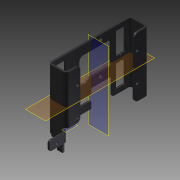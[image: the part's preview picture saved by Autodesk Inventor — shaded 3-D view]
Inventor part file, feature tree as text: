
AUTODESK INVENTOR PART (.ipt)
format: ipt  version: 2015 (Build 190159000, 159)  size: 621,056 bytes
history: native  units: mm
features: extrude x16, hole x10, fillet x7, projected_geometry x4, plane x2, other x2, mirror x1
ambient origin geometry x8: Origin, YZ Plane, XZ Plane, XY Plane, X Axis, Y Axis, Z Axis, Center Point
bodies: Solid1 (feature_tree)
feature tree (42):
  extrude  "Extrusión1"  Depth=15.0mm
  fillet  "Empalme1"  Radius=8.0mm
  extrude  "Extrusión2"  Depth=65.0mm
  hole  "Agujero1"  [1 undecoded]
  extrude  "Extrusión3"  Depth=2.0mm
  hole  "Agujero10"  [1 undecoded]
  extrude  "Extrusión21"  Depth=2.0mm
  extrude  "Extrusión22"  Depth=20.0mm
  fillet  "Empalme6"  Radius=3.0mm
  extrude  "Extrusión23"  Depth=10.11138mm TaperAngle=0.0deg
  fillet  "Empalme7"  Radius=4.0mm
  extrude  "Extrusión25"  Depth=10.11138mm
  fillet  "Empalme8"  Radius=65.0mm
  plane  "Plano de trabajo2"
  extrude  "Extrusión26"  Depth=24.2mm
  hole  "Agujero12"  [1 undecoded]
  fillet  "Empalme9"  Radius=10.0mm
  hole  "Agujero13"  [1 undecoded]
  hole  "Agujero14"  [1 undecoded]
  extrude  "Extrusión27"  Depth=35.0mm
  hole  "Agujero2"  [1 undecoded]
  hole  "Agujero3"  [1 undecoded]
  extrude  "Extrusión5"  Depth=10.0mm
  extrude  "Extrusión6"  Depth=27.0mm TaperAngle=0.0deg
  plane  "Plano de trabajo1"
  fillet  "Empalme4"  Radius=3.5mm
  mirror  "Simetría1"
  extrude  "Extrusión14"  Depth=10.0mm TaperAngle=0.0deg
  hole  "Agujero6"  [1 undecoded]
  extrude  "Extrusión18"  Depth=3.0mm
  extrude  "Extrusión19"  Depth=12.5mm
  hole  "Agujero8"  [1 undecoded]
  hole  "Agujero9"  [1 undecoded]
  fillet  "Redondeo de esquina2"  Radius=19.2mm
  extrude  "Extrusión20"  Depth=7.0mm
  other  "Desplazar cara1"
  extrude  "Extrusión16"  Depth=6.0mm
  projected_geometry  "Contorno proyectado1"
  projected_geometry  "Contorno proyectado2"
  projected_geometry  "Contorno proyectado3"
  projected_geometry  "Contorno proyectado6"
  other  "Definición1"
note: 10 required parameter values undecoded (feature->parameter linkage not recoverable at this tier; creation-order binding heuristic only, values carry confidence <= 0.55)
